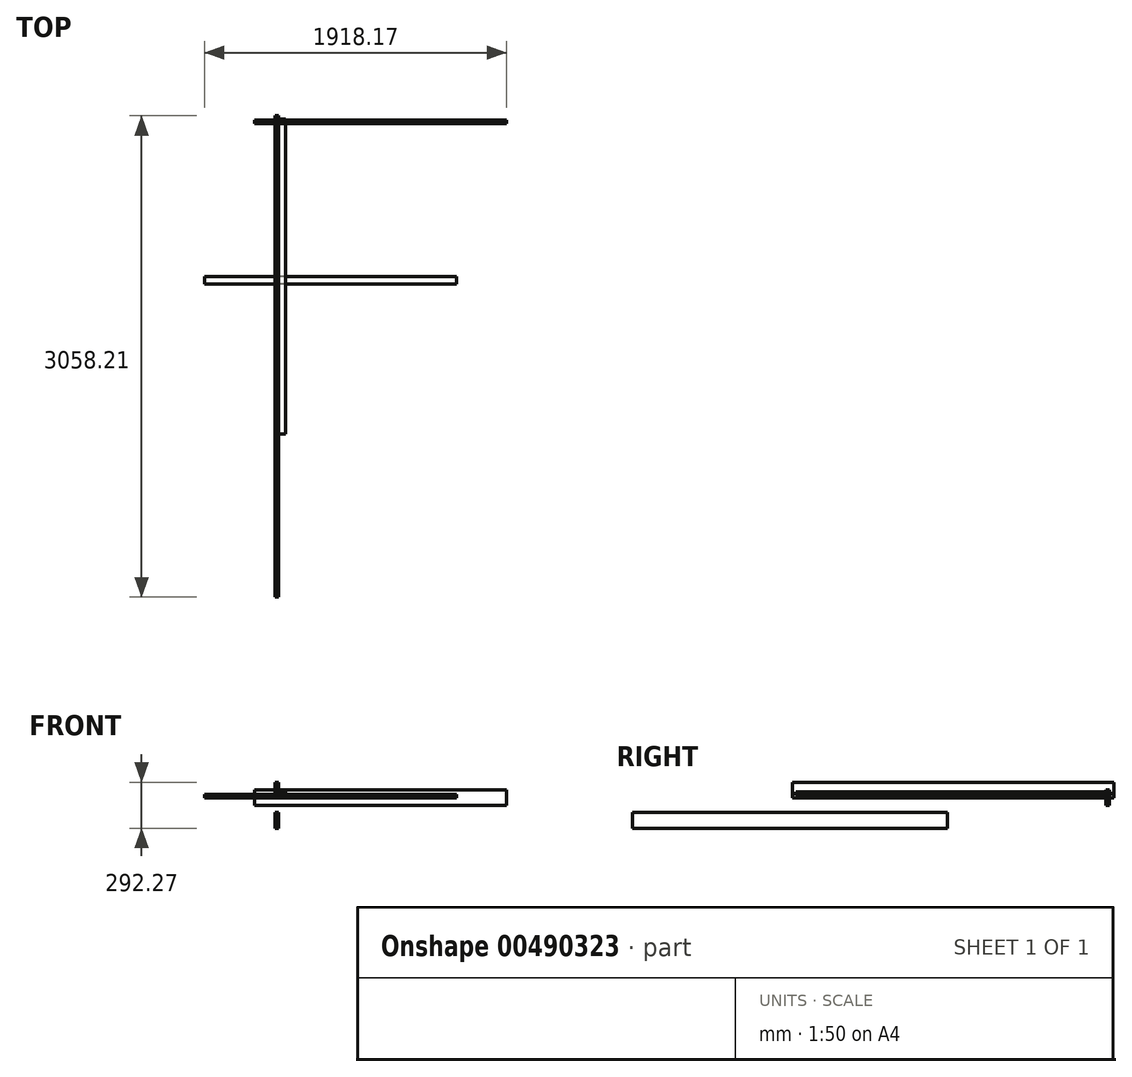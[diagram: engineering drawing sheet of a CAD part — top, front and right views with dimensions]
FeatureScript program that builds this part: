
annotation { "Feature Type Name" : "Feature", "Feature Type Description" : "" }
export const myFeature = defineFeature(function(context is Context, id is Id, definition is map)
    precondition{}
    {
        {
            assignVariable(context, id + "F0", {"name" : "width", "anyValue" : 22});
        }
        {
            var Q0;
            Q0=qCreatedBy(makeId("Right.planeOp"),FACE);
            var sketch = newSketch(context, id + "F1", { "sketchPlane" : qUnion([Q0])});
            skLineSegment(sketch, "E0.bottom", {"start": v(-2015.42, 98.94) * mm, "end": v(28.58, 98.94) * mm});
            skLineSegment(sketch, "E0.top", {"start": v(-2015.42, -1.06) * mm, "end": v(28.58, -1.06) * mm});
            skLineSegment(sketch, "E0.left", {"start": v(28.58, 98.94) * mm, "end": v(28.58, -1.06) * mm});
            skLineSegment(sketch, "E0.right", {"start": v(-2015.42, 98.94) * mm, "end": v(-2015.42, -1.06) * mm});
            skLineSegment(sketch, "E1", {"start": v(6.58, 98.94) * mm, "end": v(6.58, -1.06) * mm, "construction": true});
            skLineSegment(sketch, "E2", {"start": v(-1993.42, 98.94) * mm, "end": v(-1993.42, -1.06) * mm, "construction": true});
            skLineSegment(sketch, "E3.bottom", {"start": v(-1993.42, 14.94) * mm, "end": v(6.58, 14.94) * mm});
            skLineSegment(sketch, "E3.top", {"start": v(-1993.42, 36.94) * mm, "end": v(6.58, 36.94) * mm});
            skLineSegment(sketch, "E3.left", {"start": v(-1993.42, 14.94) * mm, "end": v(-1993.42, 36.94) * mm});
            skLineSegment(sketch, "E3.right", {"start": v(6.58, 14.94) * mm, "end": v(6.58, 36.94) * mm});
            skSolve(sketch);
        }
        {
            var Q0;
            Q0=qCreatedBy(makeId("Front.planeOp"),FACE);
            var sketch = newSketch(context, id + "F2", { "sketchPlane" : qUnion([Q0])});
            skLineSegment(sketch, "E4.bottom", {"start": v(-130.4, 50.56) * mm, "end": v(1469.6, 50.56) * mm});
            skLineSegment(sketch, "E4.top", {"start": v(-130.4, -49.44) * mm, "end": v(1469.6, -49.44) * mm});
            skLineSegment(sketch, "E4.left", {"start": v(-130.4, 50.56) * mm, "end": v(-130.4, -49.44) * mm});
            skLineSegment(sketch, "E4.right", {"start": v(1469.6, 50.56) * mm, "end": v(1469.6, -49.44) * mm});
            skSolve(sketch);
        }
        {
            var Q0;
            Q0=makeQuery(id+"F1.imprint","IMPRINT",FACE,{"disambiguationData":[TD([[makeQuery(id+"F1.imprint","IMPRINT",EDGE,{"derivedFrom":sQuery(id+"F1.wireOp",EDGE,"E0.bottom")}),-1.0]])]});
            extrude(context, id + "F3", {"entities" : qUnion([Q0]), "depth" : (getVariable(context, 'width')) * mm});
        }
        {
            var Q0;
            Q0=makeQuery(id+"F1.imprint","IMPRINT",FACE,{"disambiguationData":[TD([[makeQuery(id+"F1.imprint","IMPRINT",EDGE,{"derivedFrom":sQuery(id+"F1.wireOp",EDGE,"E3.bottom")}),1.0]])]});
            extrude(context, id + "F4", {"entities" : qUnion([Q0]), "operationType" : NewBodyOperationType.ADD, "depth" : 3 * (getVariable(context, 'width')) * mm});
        }
        {
            var Q0;
            Q0=makeQuery(id+"F2.imprint","IMPRINT",FACE,{"disambiguationData":[TD([[makeQuery(id+"F2.imprint","IMPRINT",EDGE,{"derivedFrom":sQuery(id+"F2.wireOp",EDGE,"E4.bottom")}),-1.0]])]});
            extrude(context, id + "F5", {"entities" : qUnion([Q0]), "depth" : (getVariable(context, 'width')) * mm});
        }
        {
            var Q0;
            Q0=qCreatedBy(makeId("Top.planeOp"),FACE);
            var sketch = newSketch(context, id + "F6", { "sketchPlane" : qUnion([Q0])});
            skLineSegment(sketch, "E5.bottom", {"start": v(1151.44, -1039.38) * mm, "end": v(-448.56, -1039.38) * mm});
            skLineSegment(sketch, "E5.top", {"start": v(1151.44, -994.38) * mm, "end": v(-448.56, -994.38) * mm});
            skLineSegment(sketch, "E5.left", {"start": v(1151.44, -1039.38) * mm, "end": v(1151.44, -994.38) * mm});
            skLineSegment(sketch, "E5.right", {"start": v(-448.56, -1039.38) * mm, "end": v(-448.56, -994.38) * mm});
            skSolve(sketch);
        }
        {
            var Q0;
            Q0=makeQuery(id+"F6.imprint","IMPRINT",FACE,{"disambiguationData":[TD([[makeQuery(id+"F6.imprint","IMPRINT",EDGE,{"derivedFrom":sQuery(id+"F6.wireOp",EDGE,"E5.bottom")}),-1.0]])]});
            extrude(context, id + "F7", {"entities" : qUnion([Q0]), "depth" : (getVariable(context, 'width')) * mm});
        }
        {
            var Q0;
            Q0=qCreatedBy(makeId("Right.planeOp"),FACE);
            var sketch = newSketch(context, id + "F8", { "sketchPlane" : qUnion([Q0])});
            skLineSegment(sketch, "E6.bottom", {"start": v(-1029.63, -193.33) * mm, "end": v(-3029.63, -193.33) * mm});
            skLineSegment(sketch, "E6.top", {"start": v(-1029.63, -93.33) * mm, "end": v(-3029.63, -93.33) * mm});
            skLineSegment(sketch, "E6.left", {"start": v(-1029.63, -193.33) * mm, "end": v(-1029.63, -93.33) * mm});
            skLineSegment(sketch, "E6.right", {"start": v(-3029.63, -193.33) * mm, "end": v(-3029.63, -93.33) * mm});
            skSolve(sketch);
        }
        {
            var Q0;
            Q0=makeQuery(id+"F8.imprint","IMPRINT",FACE,{"disambiguationData":[TD([[makeQuery(id+"F8.imprint","IMPRINT",EDGE,{"derivedFrom":sQuery(id+"F8.wireOp",EDGE,"E6.bottom")}),-1.0]])]});
            extrude(context, id + "F9", {"entities" : qUnion([Q0]), "depth" : (getVariable(context, 'width')) * mm});
        }
    });
